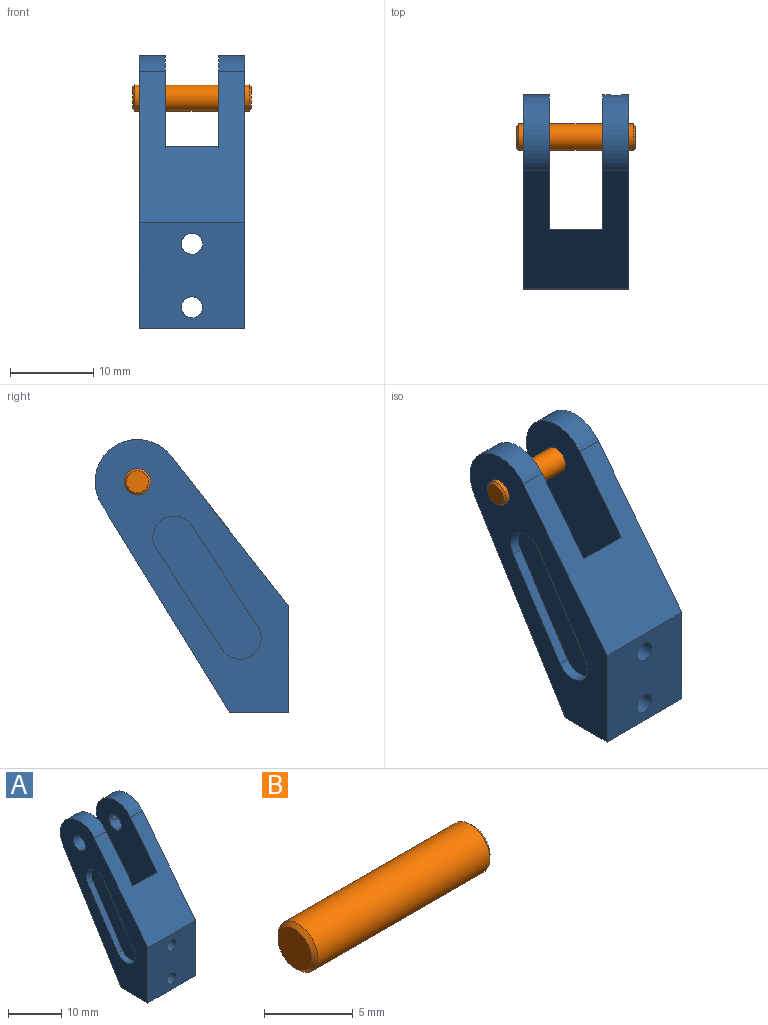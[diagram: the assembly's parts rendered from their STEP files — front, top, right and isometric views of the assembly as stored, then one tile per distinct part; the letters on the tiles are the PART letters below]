
ASSEMBLY  parts=2 mates=1
PART A: 27 faces, bbox 12.7x23.3x32.8 mm
  f0: cylinder r=5.08mm len=9.08mm, axis (1,0,0), area 46.6mm2, adj f3,f4,f12,f13,f16
  f1: cylinder r=1.59mm len=3.18mm, axis (1,0,0), area 29.5mm2, adj f12,f13,f16
  f2: cylinder r=5.08mm len=9.08mm, axis (1,0,0), area 48.5mm2, adj f3,f5,f11,f14
  f3: plane 18.12x14.19mm, normal (0,-0.79,0.62), area 218.8mm2, adj f0,f2,f9,f11,f12,f13,f14,f15
  f4: plane 25.02x15.4mm, normal (0,0.85,-0.52), area 92.5mm2, adj f0,f10,f12,f13
  f5: plane 25.02x15.4mm, normal (0,0.85,-0.52), area 92.5mm2, adj f2,f10,f11,f14
  f6: cylinder r=1.59mm len=3.18mm, axis (1,0,0), area 31.4mm2, adj f11,f14
  f7: cylinder r=1.27mm len=7.11mm, axis (0,-1,0), area 56.8mm2, adj f9,f15
  f8: cylinder r=1.27mm len=7.11mm, axis (0,-1,0), area 56.8mm2, adj f9,f15
  f9: plane 12.7x12.7mm, normal (0,-1,0), area 151.2mm2, adj f3,f7,f8,f10,f11,f12
  f10: plane 12.7x7.11mm, normal (0,0,-1), area 90.3mm2, adj f4,f5,f9,f11,f12,f15
  f11: plane 32.77x23.27mm, normal (-1,0,0), area 284.5mm2, adj f2,f3,f5,f6,f9,f10,f22,f23
  f12: plane 32.77x23.27mm, normal (1,0,0), area 284.5mm2, adj f0,f1,f3,f4,f9,f10,f17,f18
  f13: plane 32.77x16.15mm, normal (-1,0,0), area 255.6mm2, adj f0,f1,f3,f4,f15
  f14: plane 32.77x16.15mm, normal (1,0,0), area 255.6mm2, adj f2,f3,f5,f6,f15
  f15: plane 21.78x6.4mm, normal (0,1,0), area 129.3mm2, adj f3,f7,f8,f10,f13,f14
  f16: cylinder r=0.76mm len=3.69mm, axis (0,1,0), area 17mm2, adj f0,f1
  f17: plane 12.09x7.92mm, normal (0,-0.84,0.55), area 18.4mm2, adj f12,f18,f20,f21
  f18: cylinder r=2.54mm len=4.66mm, axis (1,0,0), area 10.1mm2, adj f12,f17,f19,f21
  f19: plane 12.09x7.92mm, normal (0,0.84,-0.55), area 18.4mm2, adj f12,f18,f20,f21
  f20: cylinder r=2.54mm len=4.66mm, axis (1,0,0), area 10.1mm2, adj f12,f17,f19,f21
  f21: plane 17.17x13mm, normal (1,0,0), area 93.7mm2, adj f17,f18,f19,f20
  f22: plane 12.09x7.92mm, normal (0,0.84,-0.55), area 18.4mm2, adj f11,f23,f25,f26
  f23: cylinder r=2.54mm len=4.66mm, axis (-1,0,0), area 10.1mm2, adj f11,f22,f24,f26
  f24: plane 12.09x7.92mm, normal (0,-0.84,0.55), area 18.4mm2, adj f11,f23,f25,f26
  f25: cylinder r=2.54mm len=4.66mm, axis (-1,0,0), area 10.1mm2, adj f11,f22,f24,f26
  f26: plane 17.17x13mm, normal (-1,0,0), area 93.7mm2, adj f22,f23,f24,f25
PART B: 5 faces, bbox 14.2x3.2x3.2 mm
  f0: cylinder r=1.59mm len=13.72mm, axis (-1,0,0), area 136.8mm2, adj f3,f4
  f1: plane 2.67x2.67mm, normal (1,0,0), area 5.6mm2, adj f4
  f2: plane 2.67x2.67mm, normal (-1,0,0), area 5.6mm2, adj f3
  f3: cone r=1.59mm half-angle=45deg, axis (1,0,0), area 3.3mm2, adj f0,f2
  f4: cone r=1.33mm half-angle=45deg, axis (-1,0,0), area 3.3mm2, adj f0,f1
PLACE A t=(-7.05,-6.27,3.27)mm
PLACE B t=(-20.51,78.51,7.81)mm
MATE fastened B.f0 <-> A.f0  axis (1,0,0) through (-6.29,11.92,30.96)mm
